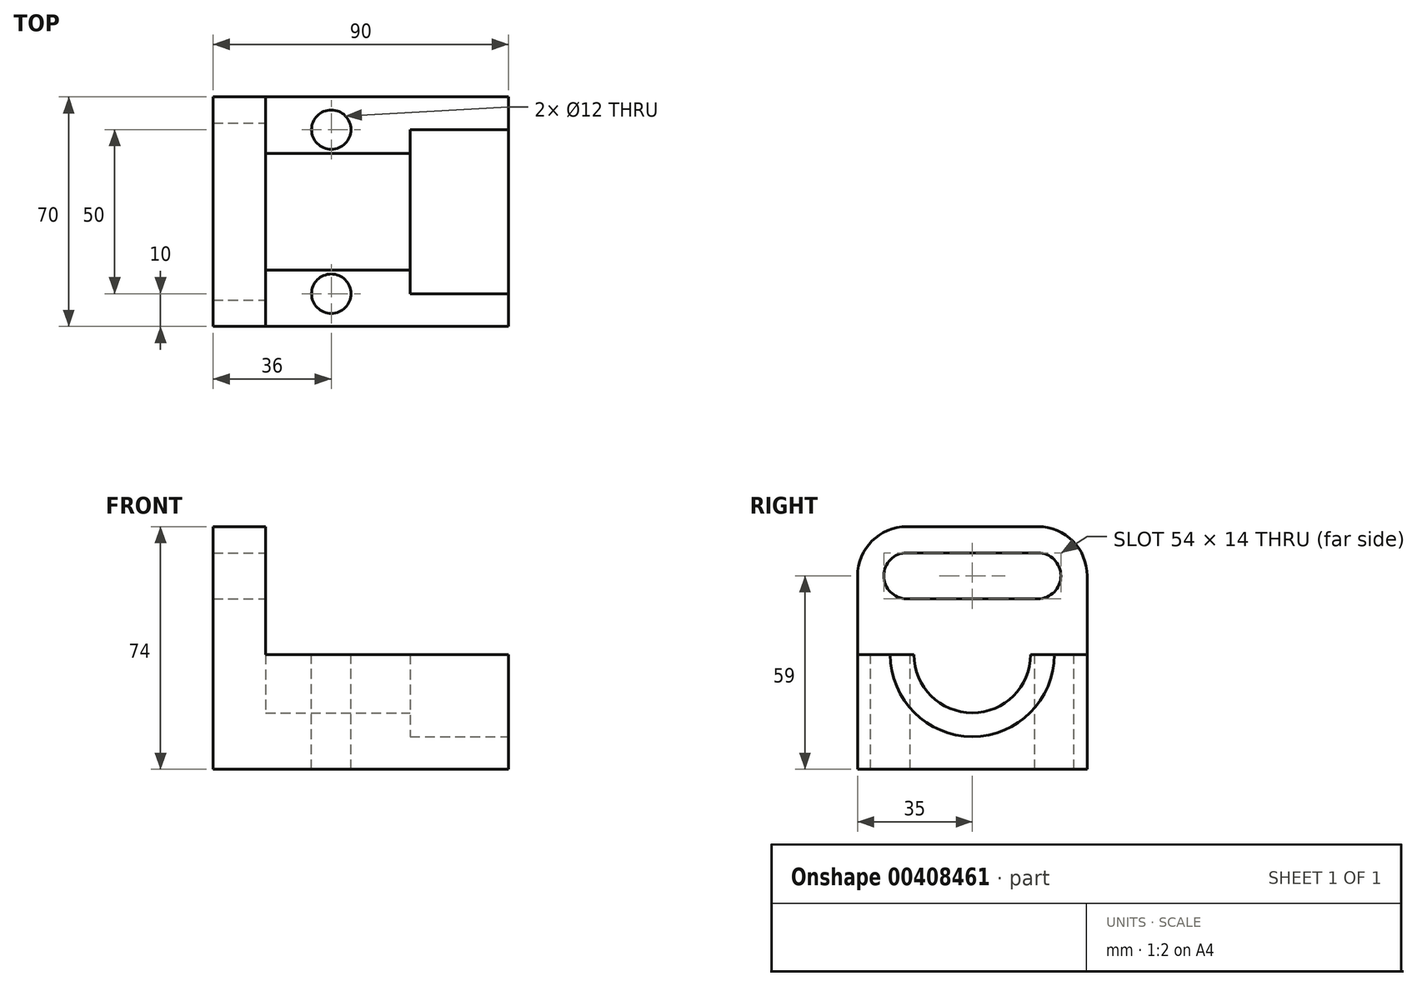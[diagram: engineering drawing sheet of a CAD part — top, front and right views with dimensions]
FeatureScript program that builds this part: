
annotation { "Feature Type Name" : "Feature", "Feature Type Description" : "" }
export const myFeature = defineFeature(function(context is Context, id is Id, definition is map)
    precondition{}
    {
        {
            var Q0;
            Q0=qCreatedBy(makeId("Front.planeOp"),FACE);
            var sketch = newSketch(context, id + "F0", { "sketchPlane" : qUnion([Q0])});
            skLineSegment(sketch, "E0", {"start": v(0, 0) * mm, "end": v(90, 0) * mm});
            skLineSegment(sketch, "E1", {"start": v(90, 0) * mm, "end": v(90, 35) * mm});
            skLineSegment(sketch, "E2", {"start": v(90, 35) * mm, "end": v(16, 35) * mm});
            skLineSegment(sketch, "E3", {"start": v(16, 35) * mm, "end": v(16, 74) * mm});
            skLineSegment(sketch, "E4", {"start": v(16, 74) * mm, "end": v(0, 74) * mm});
            skLineSegment(sketch, "E5", {"start": v(0, 74) * mm, "end": v(0, 0) * mm});
            skSolve(sketch);
        }
        {
            var Q0;
            Q0=qSketchRegion(id+"F0",true);
            extrude(context, id + "F1", {"entities" : qUnion([Q0]), "endBound" : BoundingType.SYMMETRIC, "depth" : 70 * mm});
        }
        {
            var Q0;
            Q0=makeQuery(id+"F1.opExtrude","SWEPT_FACE",FACE,{"disambiguationData":[OSD([sQuery(id+"F0.wireOp",EDGE,"E1")])]});
            var sketch = newSketch(context, id + "F2", { "sketchPlane" : qUnion([Q0])});
            skArc(sketch, "E6", {"start": v(-25, 35) * mm, "mid": v(0, 10) * mm, "end": v(25, 35) * mm});
            skLineSegment(sketch, "E7.0", {"start": v(-25, 35) * mm, "end": v(25, 35) * mm});
            skPoint(sketch, "E8.orphan", {"position": v(-35, 35) * mm});
            skPoint(sketch, "E9.orphan", {"position": v(35, 35) * mm});
            skSolve(sketch);
        }
        {
            var Q0;
            Q0=qSketchRegion(id+"F2",true);
            extrude(context, id + "F3", {"entities" : qUnion([Q0]), "operationType" : NewBodyOperationType.REMOVE, "oppositeDirection" : true, "depth" : 30 * mm});
        }
        {
            var Q0;
            Q0=makeQuery(id+"F3.boolean.opBoolean","COPY",FACE,{"derivedFrom":makeQuery(id+"F3.opExtrude","CAP_FACE",FACE,{"disambiguationData":[OSD([sQuery(id+"F2.wireOp",EDGE,"E6"),sQuery(id+"F2.wireOp",EDGE,"E7.0")])],"isStart":false})});
            var sketch = newSketch(context, id + "F4", { "sketchPlane" : qUnion([Q0])});
            skArc(sketch, "E10", {"start": v(-17.78, 35) * mm, "mid": v(0, 17.22) * mm, "end": v(17.78, 35) * mm});
            skLineSegment(sketch, "E11.0", {"start": v(-17.78, 35) * mm, "end": v(17.78, 35) * mm});
            skPoint(sketch, "E12.orphan", {"position": v(-25, 35) * mm});
            skPoint(sketch, "E13.orphan", {"position": v(25, 35) * mm});
            skSolve(sketch);
        }
        {
            var Q0;
            Q0=makeQuery(id+"F4.imprint","IMPRINT",FACE,{"disambiguationData":[TD([[makeQuery(id+"F4.imprint","IMPRINT",EDGE,{"derivedFrom":sQuery(id+"F4.wireOp",EDGE,"E10")}),1.0]])]});
            var Q1;
            Q1=makeQuery(id+"F1.opExtrude","SWEPT_FACE",FACE,{"disambiguationData":[OSD([sQuery(id+"F0.wireOp",EDGE,"E3")])]});
            extrude(context, id + "F5", {"entities" : qUnion([Q0]), "operationType" : NewBodyOperationType.REMOVE, "endBound" : BoundingType.UP_TO_SURFACE, "oppositeDirection" : true, "endBoundEntityFace" : qUnion([Q1]), "depth" : 25 * mm});
        }
        {
            var Q0;
            Q0=makeQuery(id+"F1.opExtrude","CAP_EDGE",EDGE,{"disambiguationData":[OSD([sQuery(id+"F0.wireOp",EDGE,"E4")])],"isStart":false});
            var Q1;
            Q1=makeQuery(id+"F1.opExtrude","CAP_EDGE",EDGE,{"disambiguationData":[OSD([sQuery(id+"F0.wireOp",EDGE,"E4")])],"isStart":true});
            fillet(context, id + "F6", {"entities" : qUnion([Q0, Q1]), "radius" : 15 * mm, "tangentPropagation" : true, "allowEdgeOverflow" : false});
        }
        {
            var Q0;
            {var subQ0=sQuery(id+"F0.wireOp",EDGE,"E3");Q0=makeQuery(id+"F5.boolean.opBoolean","MERGE",FACE,{"derivedFrom":[makeQuery(id+"F1.opExtrude","SWEPT_FACE",FACE,{"disambiguationData":[OSD([subQ0])]}),makeQuery(id+"F5.opExtrude","CAP_FACE",FACE,{"disambiguationData":[OSD([subQ0])],"isStart":false})]});}
            var sketch = newSketch(context, id + "F7", { "sketchPlane" : qUnion([Q0])});
            skArc(sketch, "E14.0.startCap", {"start": v(-20, 52) * mm, "mid": v(-27, 59) * mm, "end": v(-20, 66) * mm});
            skArc(sketch, "E14.0.endCap", {"start": v(20, 66) * mm, "mid": v(27, 59) * mm, "end": v(20, 52) * mm});
            skLineSegment(sketch, "E14.0.left", {"start": v(-20, 66) * mm, "end": v(20, 66) * mm});
            skLineSegment(sketch, "E14.0.right", {"start": v(-20, 52) * mm, "end": v(20, 52) * mm});
            skSolve(sketch);
        }
        {
            var Q0;
            Q0=qSketchRegion(id+"F7",true);
            extrude(context, id + "F8", {"entities" : qUnion([Q0]), "operationType" : NewBodyOperationType.REMOVE, "endBound" : BoundingType.THROUGH_ALL, "oppositeDirection" : true, "depth" : 25 * mm});
        }
        {
            var Q0;
            {var subQ1=sQuery(id+"F0.wireOp",EDGE,"E3");var subQ2=sQuery(id+"F0.wireOp",EDGE,"E1");var subQ3=sQuery(id+"F0.wireOp",EDGE,"E2");Q0=makeQuery(id+"F5.boolean.opBoolean","SPLIT",FACE,{"disambiguationData":[TD([makeQuery(id+"F1.opExtrude","CAP_FACE",FACE,{"disambiguationData":[OSD([sQuery(id+"F0.wireOp",EDGE,"E0"),subQ2,subQ3,subQ1,sQuery(id+"F0.wireOp",EDGE,"E4"),sQuery(id+"F0.wireOp",EDGE,"E5")])],"isStart":false})])],"derivedFrom":makeQuery(id+"F1.opExtrude","SWEPT_FACE",FACE,{"disambiguationData":[OSD([subQ3])]})});}
            var sketch = newSketch(context, id + "F9", { "sketchPlane" : qUnion([Q0])});
            skCircle(sketch, "E15", {"center": v(36, -25) * mm, "radius": 6 * mm});
            skCircle(sketch, "E16.MirrorC", {"center": v(36, 25) * mm, "radius": 6 * mm});
            skSolve(sketch);
        }
        {
            var Q0;
            Q0=qSketchRegion(id+"F9",true);
            extrude(context, id + "F10", {"entities" : qUnion([Q0]), "operationType" : NewBodyOperationType.REMOVE, "endBound" : BoundingType.THROUGH_ALL, "oppositeDirection" : true, "depth" : 25 * mm});
        }
    });
